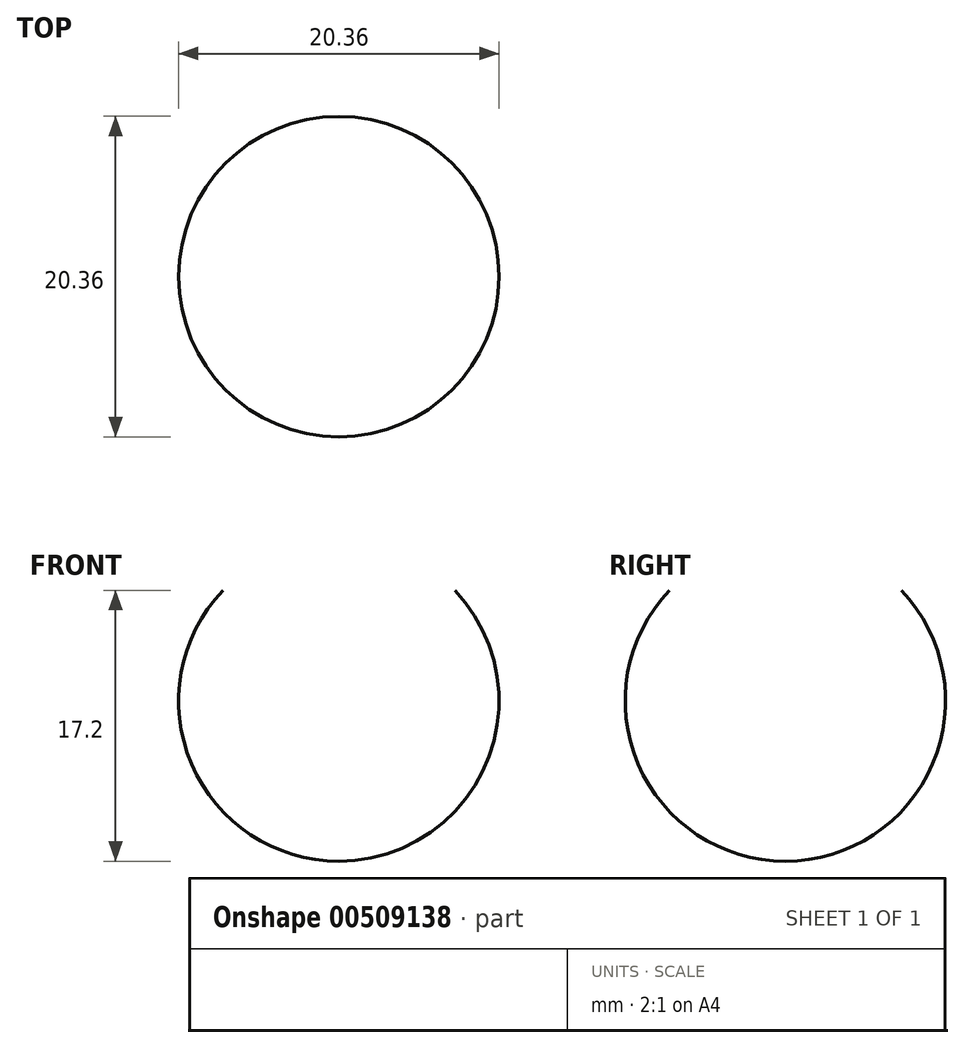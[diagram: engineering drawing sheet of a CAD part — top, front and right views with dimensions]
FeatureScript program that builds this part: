
annotation { "Feature Type Name" : "Feature", "Feature Type Description" : "" }
export const myFeature = defineFeature(function(context is Context, id is Id, definition is map)
    precondition{}
    {
        {
            var Q0;
            Q0=qCreatedBy(makeId("Front.planeOp"),FACE);
            var sketch = newSketch(context, id + "F0", { "sketchPlane" : qUnion([Q0])});
            skLineSegment(sketch, "E0", {"start": v(0, 0) * mm, "end": v(0, 35.6) * mm, "construction": true});
            skArc(sketch, "E1", {"start": v(0, 35.6) * mm, "mid": v(1.9, 25.69) * mm, "end": v(7.37, 17.2) * mm});
            skArc(sketch, "E2", {"start": v(0, 0) * mm, "mid": v(9.35, 6.17) * mm, "end": v(7.37, 17.2) * mm});
            skLineSegment(sketch, "E3", {"start": v(0, 35.6) * mm, "end": v(0, 0) * mm});
            skLineSegment(sketch, "E4", {"start": v(0, 0) * mm, "end": v(0, 55.98) * mm, "construction": true});
            skSolve(sketch);
        }
        {
            var Q0;
            Q0 = qSketchRegion(id + "F0", true);
            var Q1;
            Q1=sQuery(id+"F0.wireOp",EDGE,"E3");
            revolve(context, id + "F1", {"entities" : qUnion([Q0]), "axis" : qUnion([Q1]), "revolveType" : RevolveType.FULL});
        }
    });
